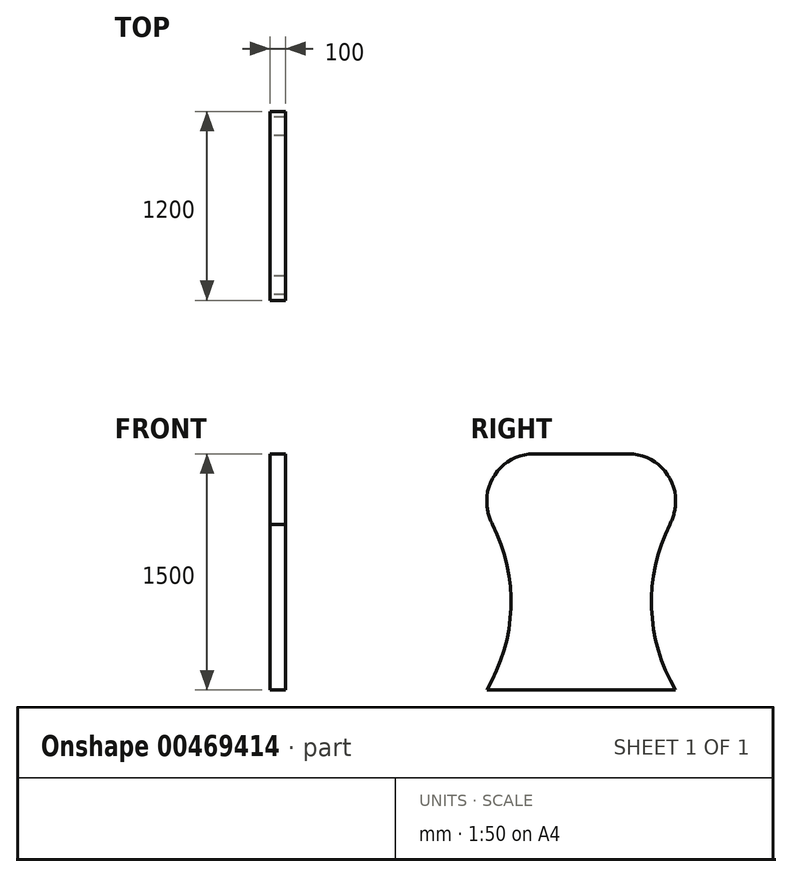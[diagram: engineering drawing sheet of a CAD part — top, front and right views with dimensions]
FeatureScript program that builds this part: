
annotation { "Feature Type Name" : "Feature", "Feature Type Description" : "" }
export const myFeature = defineFeature(function(context is Context, id is Id, definition is map)
    precondition{}
    {
        {
            var Q0;
            Q0=qCreatedBy(makeId("Right.planeOp"),FACE);
            var sketch = newSketch(context, id + "F0", { "sketchPlane" : qUnion([Q0])});
            skLineSegment(sketch, "E0.bottom", {"start": v(0, 0) * mm, "end": v(-600, 0) * mm});
            skLineSegment(sketch, "E0.top", {"start": v(0, 1500) * mm, "end": v(-300, 1500) * mm});
            skLineSegment(sketch, "E0.left", {"start": v(0, 0) * mm, "end": v(0, 1500) * mm, "construction": true});
            skLineSegment(sketch, "E0.right", {"start": v(-600, 0) * mm, "end": v(-600, 1200) * mm, "construction": true});
            skPoint(sketch, "E1.visualSharp", {"position": v(-600, 1500) * mm});
            skArc(sketch, "E1.filletArc", {"start": v(-300, 1500) * mm, "mid": v(-512.13, 1412.13) * mm, "end": v(-600, 1200) * mm});
            skArc(sketch, "E2", {"start": v(-600, 0) * mm, "mid": v(-446.75, 521.36) * mm, "end": v(-563.05, 1052.18) * mm});
            skArc(sketch, "E3", {"start": v(-600, 1200) * mm, "mid": v(-590.62, 1123.82) * mm, "end": v(-563.05, 1052.18) * mm});
            skArc(sketch, "E4.MirrorCS", {"start": v(600, 0) * mm, "mid": v(446.75, 521.36) * mm, "end": v(563.05, 1052.18) * mm});
            skLineSegment(sketch, "E5.MirrorCS", {"start": v(0, 1500) * mm, "end": v(300, 1500) * mm});
            skLineSegment(sketch, "E6.MirrorCS", {"start": v(600, 0) * mm, "end": v(600, 1200) * mm, "construction": true});
            skArc(sketch, "E7.MirrorCS", {"start": v(300, 1500) * mm, "mid": v(512.13, 1412.13) * mm, "end": v(600, 1200) * mm});
            skLineSegment(sketch, "E8.MirrorCS", {"start": v(0, 0) * mm, "end": v(600, 0) * mm});
            skPoint(sketch, "E9.MirrorP", {"position": v(600, 1500) * mm});
            skArc(sketch, "E10.MirrorCS", {"start": v(600, 1200) * mm, "mid": v(590.62, 1123.82) * mm, "end": v(563.05, 1052.18) * mm});
            skSolve(sketch);
        }
        {
            var Q0;
            Q0=makeQuery(id+"F0.imprint","IMPRINT",FACE,{"disambiguationData":[TD([[makeQuery(id+"F0.imprint","IMPRINT",EDGE,{"derivedFrom":sQuery(id+"F0.wireOp",EDGE,"E0.bottom")}),-1.0]])]});
            extrude(context, id + "F1", {"entities" : qUnion([Q0]), "depth" : 100 * mm, "symmetric" : true});
        }
    });
